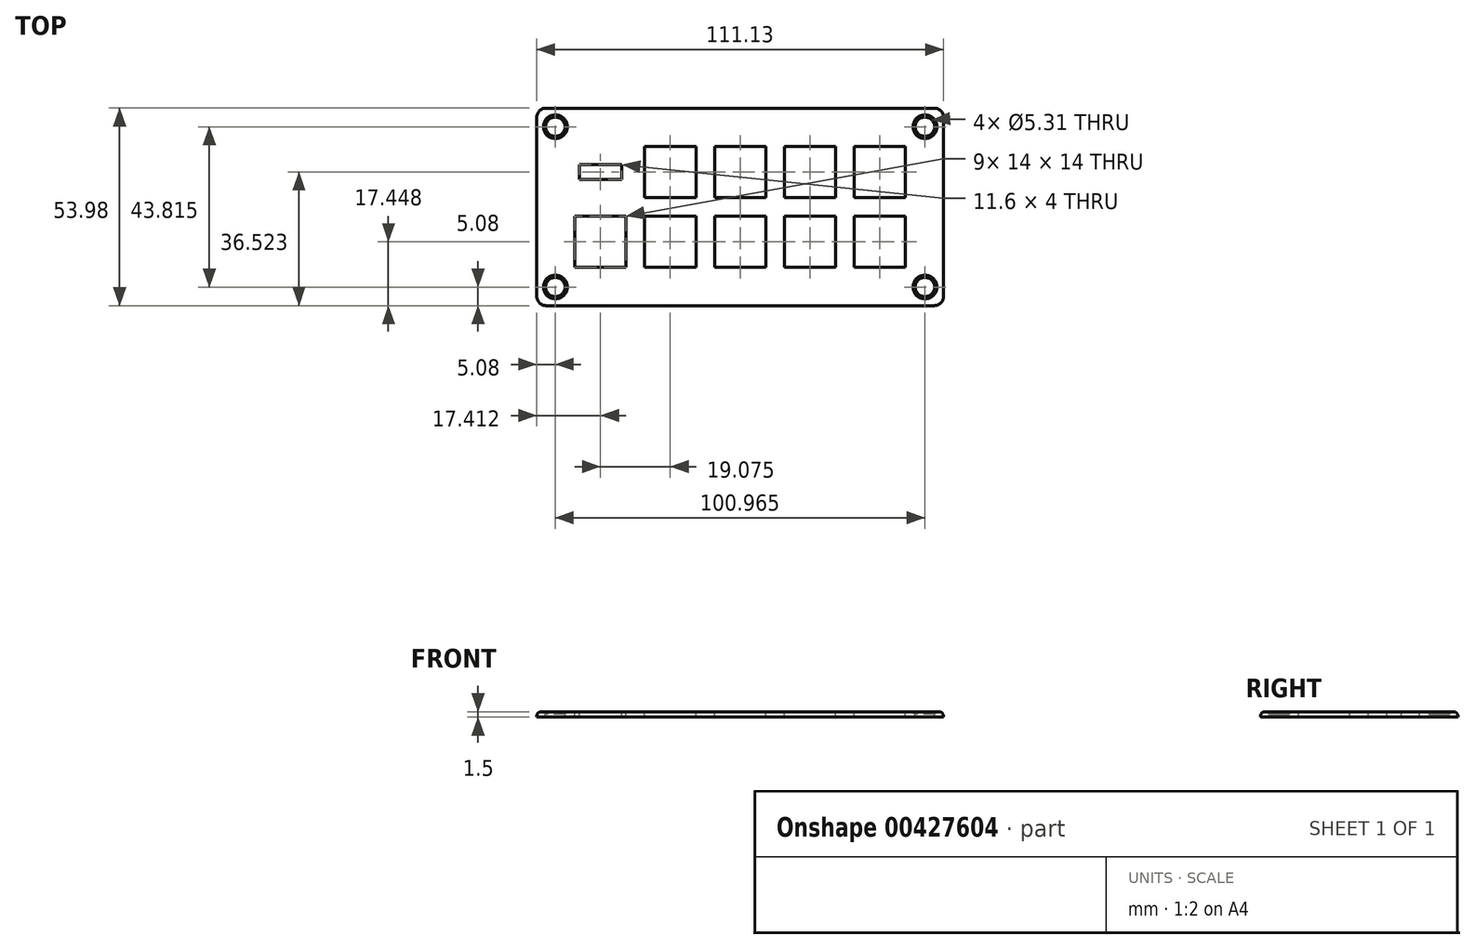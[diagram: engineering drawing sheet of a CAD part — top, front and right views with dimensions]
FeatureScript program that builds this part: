
annotation { "Feature Type Name" : "Feature", "Feature Type Description" : "" }
export const myFeature = defineFeature(function(context is Context, id is Id, definition is map)
    precondition{}
    {
        {
            var Q0;
            Q0=qCreatedBy(makeId("Top.planeOp"),FACE);
            var sketch = newSketch(context, id + "F0", { "sketchPlane" : qUnion([Q0])});
            skLineSegment(sketch, "E0.bottom", {"start": v(2.54, 0) * mm, "end": v(108.59, 0) * mm});
            skLineSegment(sketch, "E0.top", {"start": v(2.54, 53.98) * mm, "end": v(108.59, 53.98) * mm});
            skLineSegment(sketch, "E0.left", {"start": v(0, 2.54) * mm, "end": v(0, 51.44) * mm});
            skLineSegment(sketch, "E0.right", {"start": v(111.12, 2.54) * mm, "end": v(111.12, 51.44) * mm});
            skPoint(sketch, "E1.visualSharp", {"position": v(0, 53.98) * mm});
            skArc(sketch, "E1.filletArc", {"start": v(2.54, 53.98) * mm, "mid": v(0.74, 53.23) * mm, "end": v(0, 51.44) * mm});
            skPoint(sketch, "E2.visualSharp", {"position": v(111.12, 53.98) * mm});
            skArc(sketch, "E2.filletArc", {"start": v(111.12, 51.44) * mm, "mid": v(110.38, 53.23) * mm, "end": v(108.59, 53.98) * mm});
            skPoint(sketch, "E3.visualSharp", {"position": v(111.12, 0) * mm});
            skArc(sketch, "E3.filletArc", {"start": v(108.59, 0) * mm, "mid": v(110.38, 0.74) * mm, "end": v(111.13, 2.54) * mm});
            skPoint(sketch, "E4.visualSharp", {"position": v(0, 0) * mm});
            skArc(sketch, "E4.filletArc", {"start": v(0, 2.54) * mm, "mid": v(0.74, 0.74) * mm, "end": v(2.54, 0) * mm});
            skLineSegment(sketch, "E5", {"start": v(0, 26.99) * mm, "end": v(111.12, 26.99) * mm, "construction": true});
            skLineSegment(sketch, "E6", {"start": v(55.56, 53.98) * mm, "end": v(55.56, 0) * mm, "construction": true});
            skLineSegment(sketch, "E7.bottom", {"start": v(62.56, 24.45) * mm, "end": v(48.56, 24.45) * mm});
            skLineSegment(sketch, "E7.top", {"start": v(62.56, 10.45) * mm, "end": v(48.56, 10.45) * mm});
            skLineSegment(sketch, "E7.left", {"start": v(62.56, 24.45) * mm, "end": v(62.56, 10.45) * mm});
            skLineSegment(sketch, "E7.right", {"start": v(48.56, 24.45) * mm, "end": v(48.56, 10.45) * mm});
            skPoint(sketch, "E7.middle", {"position": v(55.56, 17.45) * mm});
            skLineSegment(sketch, "E8.0.1.0", {"start": v(62.56, 43.52) * mm, "end": v(48.56, 43.52) * mm});
            skLineSegment(sketch, "E8.0.1.1", {"start": v(48.56, 43.52) * mm, "end": v(48.56, 29.52) * mm});
            skLineSegment(sketch, "E8.0.1.2", {"start": v(62.56, 29.52) * mm, "end": v(48.56, 29.52) * mm});
            skLineSegment(sketch, "E8.0.1.3", {"start": v(62.56, 43.52) * mm, "end": v(62.56, 29.52) * mm});
            skLineSegment(sketch, "E8.1.0.0", {"start": v(81.64, 24.45) * mm, "end": v(67.64, 24.45) * mm});
            skLineSegment(sketch, "E8.1.0.1", {"start": v(67.64, 24.45) * mm, "end": v(67.64, 10.45) * mm});
            skLineSegment(sketch, "E8.1.0.2", {"start": v(81.64, 10.45) * mm, "end": v(67.64, 10.45) * mm});
            skLineSegment(sketch, "E8.1.0.3", {"start": v(81.64, 24.45) * mm, "end": v(81.64, 10.45) * mm});
            skLineSegment(sketch, "E8.1.1.0", {"start": v(81.64, 43.52) * mm, "end": v(67.64, 43.52) * mm});
            skLineSegment(sketch, "E8.1.1.1", {"start": v(67.64, 43.52) * mm, "end": v(67.64, 29.52) * mm});
            skLineSegment(sketch, "E8.1.1.2", {"start": v(81.64, 29.52) * mm, "end": v(67.64, 29.52) * mm});
            skLineSegment(sketch, "E8.1.1.3", {"start": v(81.64, 43.52) * mm, "end": v(81.64, 29.52) * mm});
            skLineSegment(sketch, "E8.2.0.0", {"start": v(100.71, 24.45) * mm, "end": v(86.71, 24.45) * mm});
            skLineSegment(sketch, "E8.2.0.1", {"start": v(86.71, 24.45) * mm, "end": v(86.71, 10.45) * mm});
            skLineSegment(sketch, "E8.2.0.2", {"start": v(100.71, 10.45) * mm, "end": v(86.71, 10.45) * mm});
            skLineSegment(sketch, "E8.2.0.3", {"start": v(100.71, 24.45) * mm, "end": v(100.71, 10.45) * mm});
            skLineSegment(sketch, "E8.2.1.0", {"start": v(100.71, 43.52) * mm, "end": v(86.71, 43.52) * mm});
            skLineSegment(sketch, "E8.2.1.1", {"start": v(86.71, 43.52) * mm, "end": v(86.71, 29.52) * mm});
            skLineSegment(sketch, "E8.2.1.2", {"start": v(100.71, 29.52) * mm, "end": v(86.71, 29.52) * mm});
            skLineSegment(sketch, "E8.2.1.3", {"start": v(100.71, 43.52) * mm, "end": v(100.71, 29.52) * mm});
            skLineSegment(sketch, "E8.direction1", {"start": v(48.56, 24.45) * mm, "end": v(67.64, 24.45) * mm, "construction": true});
            skLineSegment(sketch, "E8.direction2", {"start": v(48.56, 24.45) * mm, "end": v(48.56, 43.52) * mm, "construction": true});
            skLineSegment(sketch, "E9.MirrorCS", {"start": v(29.49, 29.52) * mm, "end": v(43.49, 29.52) * mm});
            skLineSegment(sketch, "E10.MirrorCS", {"start": v(10.41, 10.45) * mm, "end": v(24.41, 10.45) * mm});
            skLineSegment(sketch, "E11.MirrorCS", {"start": v(10.41, 24.45) * mm, "end": v(24.41, 24.45) * mm});
            skLineSegment(sketch, "E12.MirrorCS", {"start": v(29.49, 24.45) * mm, "end": v(29.49, 10.45) * mm});
            skLineSegment(sketch, "E13.MirrorCS", {"start": v(10.41, 24.45) * mm, "end": v(10.41, 10.45) * mm});
            skLineSegment(sketch, "E14.MirrorCS", {"start": v(29.49, 10.45) * mm, "end": v(43.49, 10.45) * mm});
            skLineSegment(sketch, "E15.MirrorCS", {"start": v(43.49, 43.52) * mm, "end": v(43.49, 29.52) * mm});
            skLineSegment(sketch, "E16.MirrorCS", {"start": v(24.41, 24.45) * mm, "end": v(24.41, 10.45) * mm});
            skLineSegment(sketch, "E17.MirrorCS", {"start": v(43.49, 24.45) * mm, "end": v(43.49, 10.45) * mm});
            skLineSegment(sketch, "E18.MirrorCS", {"start": v(29.49, 24.45) * mm, "end": v(43.49, 24.45) * mm});
            skLineSegment(sketch, "E19.MirrorCS", {"start": v(29.49, 43.52) * mm, "end": v(43.49, 43.52) * mm});
            skLineSegment(sketch, "E20.MirrorCS", {"start": v(29.49, 43.52) * mm, "end": v(29.49, 29.52) * mm});
            skLineSegment(sketch, "E21.bottom", {"start": v(11.61, 38.52) * mm, "end": v(23.21, 38.52) * mm});
            skLineSegment(sketch, "E21.top", {"start": v(11.61, 34.52) * mm, "end": v(23.21, 34.52) * mm});
            skLineSegment(sketch, "E21.left", {"start": v(11.61, 38.52) * mm, "end": v(11.61, 34.52) * mm});
            skLineSegment(sketch, "E21.right", {"start": v(23.21, 38.52) * mm, "end": v(23.21, 34.52) * mm});
            skPoint(sketch, "E21.middle", {"position": v(17.41, 36.52) * mm});
            skLineSegment(sketch, "E22", {"start": v(17.41, 24.45) * mm, "end": v(17.41, 36.52) * mm, "construction": true});
            skLineSegment(sketch, "E23", {"start": v(43.49, 36.52) * mm, "end": v(17.41, 36.52) * mm, "construction": true});
            skPoint(sketch, "E24", {"position": v(5.08, 48.9) * mm});
            skLineSegment(sketch, "E25", {"start": v(5.08, 48.9) * mm, "end": v(5.08, 53.98) * mm, "construction": true});
            skLineSegment(sketch, "E26", {"start": v(5.08, 48.9) * mm, "end": v(0, 48.9) * mm, "construction": true});
            skPoint(sketch, "E27.MirrorP", {"position": v(106.04, 48.9) * mm});
            skPoint(sketch, "E28.MirrorP", {"position": v(5.08, 5.08) * mm});
            skPoint(sketch, "E29.MirrorP", {"position": v(106.04, 5.08) * mm});
            skSolve(sketch);
        }
        {
            var Q0;
            Q0=makeQuery(id+"F0.imprint","IMPRINT",FACE,{"disambiguationData":[TD([[makeQuery(id+"F0.imprint","IMPRINT",EDGE,{"derivedFrom":sQuery(id+"F0.wireOp",EDGE,"E0.bottom")}),1.0]])]});
            extrude(context, id + "F1", {"entities" : qUnion([Q0]), "oppositeDirection" : true, "depth" : 1.5 * mm});
        }
        {
            var Q0;
            Q0=sQuery(id+"F0.wireOp",VERTEX,"E24");
            var Q1;
            Q1=sQuery(id+"F0.wireOp",VERTEX,"E28.MirrorP");
            var Q2;
            Q2=sQuery(id+"F0.wireOp",VERTEX,"E29.MirrorP");
            var Q3;
            Q3=sQuery(id+"F0.wireOp",VERTEX,"E27.MirrorP");
            var Q4;
            Q4=makeQuery(id+"F1.opExtrude","SWEPT_BODY",BODY,{"disambiguationData":[OSD([sQuery(id+"F0.wireOp",EDGE,"E0.bottom"),sQuery(id+"F0.wireOp",EDGE,"E0.top"),sQuery(id+"F0.wireOp",EDGE,"E0.left"),sQuery(id+"F0.wireOp",EDGE,"E0.right"),sQuery(id+"F0.wireOp",EDGE,"E1.filletArc"),sQuery(id+"F0.wireOp",EDGE,"E2.filletArc"),sQuery(id+"F0.wireOp",EDGE,"E3.filletArc"),sQuery(id+"F0.wireOp",EDGE,"E4.filletArc"),sQuery(id+"F0.wireOp",EDGE,"E7.bottom"),sQuery(id+"F0.wireOp",EDGE,"E7.top"),sQuery(id+"F0.wireOp",EDGE,"E7.left"),sQuery(id+"F0.wireOp",EDGE,"E7.right"),sQuery(id+"F0.wireOp",EDGE,"E8.0.1.0"),sQuery(id+"F0.wireOp",EDGE,"E8.0.1.1"),sQuery(id+"F0.wireOp",EDGE,"E8.0.1.2"),sQuery(id+"F0.wireOp",EDGE,"E8.0.1.3"),sQuery(id+"F0.wireOp",EDGE,"E8.1.0.0"),sQuery(id+"F0.wireOp",EDGE,"E8.1.0.1"),sQuery(id+"F0.wireOp",EDGE,"E8.1.0.2"),sQuery(id+"F0.wireOp",EDGE,"E8.1.0.3"),sQuery(id+"F0.wireOp",EDGE,"E8.1.1.0"),sQuery(id+"F0.wireOp",EDGE,"E8.1.1.1"),sQuery(id+"F0.wireOp",EDGE,"E8.1.1.2"),sQuery(id+"F0.wireOp",EDGE,"E8.1.1.3"),sQuery(id+"F0.wireOp",EDGE,"E8.2.0.0"),sQuery(id+"F0.wireOp",EDGE,"E8.2.0.1"),sQuery(id+"F0.wireOp",EDGE,"E8.2.0.2"),sQuery(id+"F0.wireOp",EDGE,"E8.2.0.3"),sQuery(id+"F0.wireOp",EDGE,"E8.2.1.0"),sQuery(id+"F0.wireOp",EDGE,"E8.2.1.1"),sQuery(id+"F0.wireOp",EDGE,"E8.2.1.2"),sQuery(id+"F0.wireOp",EDGE,"E8.2.1.3"),sQuery(id+"F0.wireOp",EDGE,"E9.MirrorCS"),sQuery(id+"F0.wireOp",EDGE,"E10.MirrorCS"),sQuery(id+"F0.wireOp",EDGE,"E11.MirrorCS"),sQuery(id+"F0.wireOp",EDGE,"E12.MirrorCS"),sQuery(id+"F0.wireOp",EDGE,"E13.MirrorCS"),sQuery(id+"F0.wireOp",EDGE,"E14.MirrorCS"),sQuery(id+"F0.wireOp",EDGE,"E15.MirrorCS"),sQuery(id+"F0.wireOp",EDGE,"E16.MirrorCS"),sQuery(id+"F0.wireOp",EDGE,"E17.MirrorCS"),sQuery(id+"F0.wireOp",EDGE,"E18.MirrorCS"),sQuery(id+"F0.wireOp",EDGE,"E19.MirrorCS"),sQuery(id+"F0.wireOp",EDGE,"E20.MirrorCS"),sQuery(id+"F0.wireOp",EDGE,"E21.bottom"),sQuery(id+"F0.wireOp",EDGE,"E21.top"),sQuery(id+"F0.wireOp",EDGE,"E21.left"),sQuery(id+"F0.wireOp",EDGE,"E21.right")])]});
            hole(context, id + "F2", {"style" : HoleStyle.C_SINK, "endStyle" : HoleEndStyle.THROUGH, "standardTappedOrClearance" : lookupTablePath({ "standard" : "ANSI", "size" : "#4 (0.2)", "type" : "Drilled" }), "standardBlindInLast" : lookupTablePath({ "standard" : "ANSI", "size" : "#4", "type" : "Drilled" }), "holeDiameter" : 5.3 * mm, "cSinkDiameter" : 6.48 * mm, "cSinkAngle" : 82 * degree, "isTappedThrough" : true, "tappedDepth" : 12.7 * mm, "tapClearance" : 3, "locations" : qUnion([Q0, Q1, Q2, Q3]), "scope" : qUnion([Q4])});
        }
        {
            var Q0;
            Q0=makeQuery(id+"F1.opExtrude","CAP_EDGE",EDGE,{"disambiguationData":[OSD([sQuery(id+"F0.wireOp",EDGE,"E0.bottom")])],"isStart":true});
            var Q1;
            Q1=makeQuery(id+"F1.opExtrude","CAP_EDGE",EDGE,{"disambiguationData":[OSD([sQuery(id+"F0.wireOp",EDGE,"E0.right")])],"isStart":true});
            var Q2;
            Q2=makeQuery(id+"F1.opExtrude","CAP_EDGE",EDGE,{"disambiguationData":[OSD([sQuery(id+"F0.wireOp",EDGE,"E3.filletArc")])],"isStart":true});
            var Q3;
            Q3=makeQuery(id+"F1.opExtrude","CAP_EDGE",EDGE,{"disambiguationData":[OSD([sQuery(id+"F0.wireOp",EDGE,"E2.filletArc")])],"isStart":true});
            var Q4;
            Q4=makeQuery(id+"F1.opExtrude","CAP_EDGE",EDGE,{"disambiguationData":[OSD([sQuery(id+"F0.wireOp",EDGE,"E0.top")])],"isStart":true});
            var Q5;
            Q5=makeQuery(id+"F1.opExtrude","CAP_EDGE",EDGE,{"disambiguationData":[OSD([sQuery(id+"F0.wireOp",EDGE,"E1.filletArc")])],"isStart":true});
            var Q6;
            Q6=makeQuery(id+"F1.opExtrude","CAP_EDGE",EDGE,{"disambiguationData":[OSD([sQuery(id+"F0.wireOp",EDGE,"E0.left")])],"isStart":true});
            var Q7;
            Q7=makeQuery(id+"F1.opExtrude","CAP_EDGE",EDGE,{"disambiguationData":[OSD([sQuery(id+"F0.wireOp",EDGE,"E4.filletArc")])],"isStart":true});
            fillet(context, id + "F3", {"entities" : qUnion([Q0, Q1, Q2, Q3, Q4, Q5, Q6, Q7]), "radius" : 1.27 * mm, "tangentPropagation" : true, "allowEdgeOverflow" : false});
        }
    });
